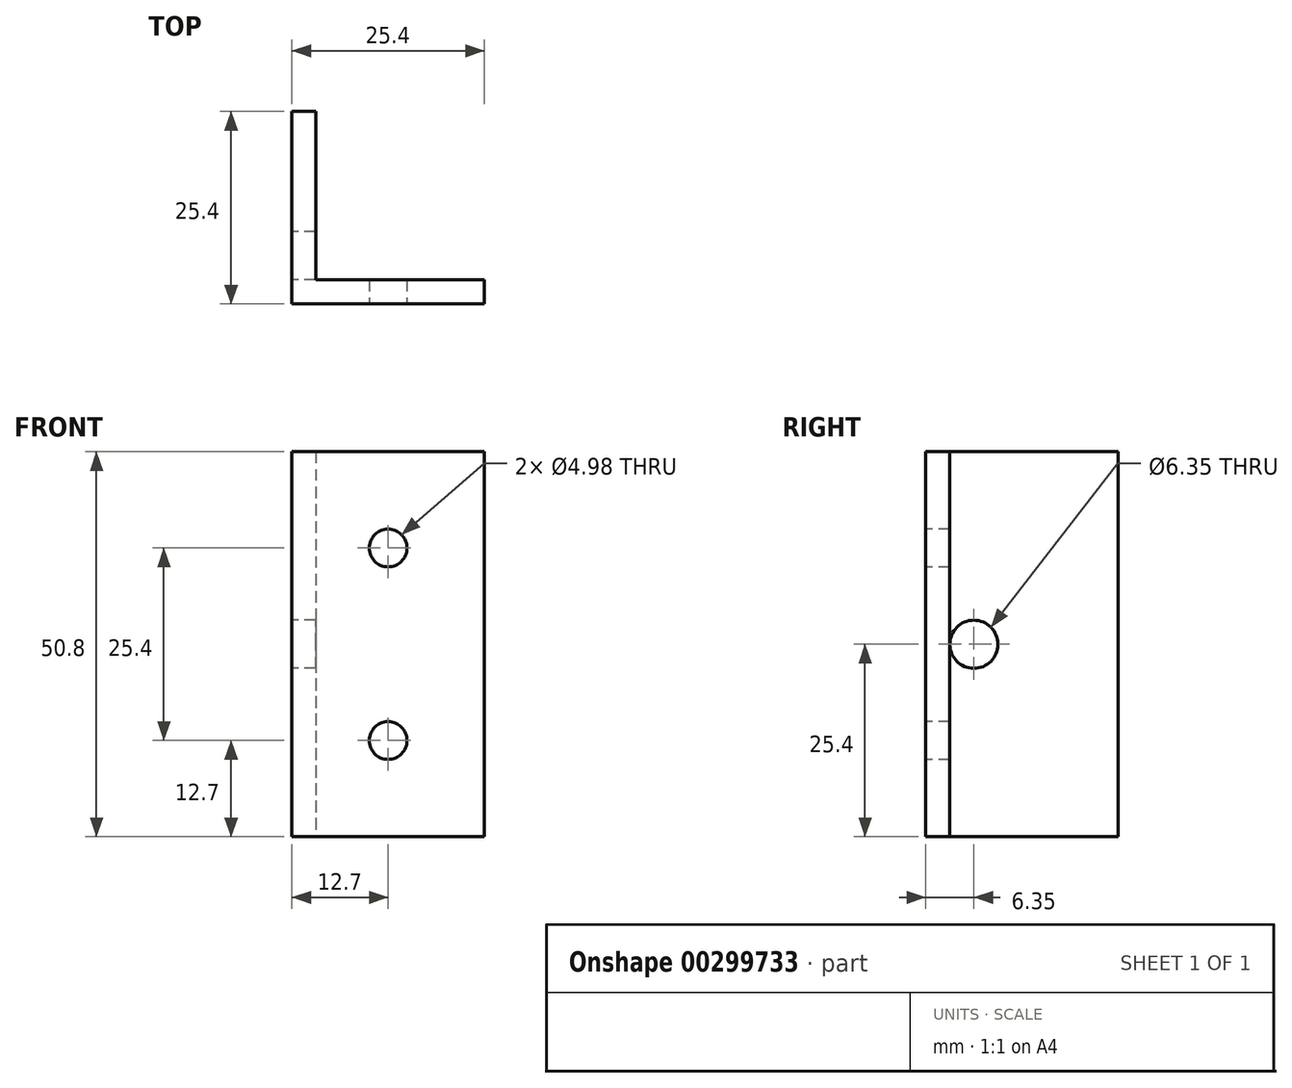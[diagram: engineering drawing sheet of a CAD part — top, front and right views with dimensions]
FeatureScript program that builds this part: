
annotation { "Feature Type Name" : "Feature", "Feature Type Description" : "" }
export const myFeature = defineFeature(function(context is Context, id is Id, definition is map)
    precondition{}
    {
        {
            var Q0;
            Q0=qCreatedBy(makeId("Top.planeOp"),FACE);
            var sketch = newSketch(context, id + "F0", { "sketchPlane" : qUnion([Q0])});
            skLineSegment(sketch, "E0", {"start": v(0, 25.4) * mm, "end": v(0, 0) * mm});
            skLineSegment(sketch, "E1", {"start": v(0, 0) * mm, "end": v(25.4, 0) * mm});
            skLineSegment(sketch, "E2", {"start": v(25.4, 0) * mm, "end": v(25.4, 3.18) * mm});
            skLineSegment(sketch, "E3", {"start": v(25.4, 3.18) * mm, "end": v(3.18, 3.17) * mm});
            skLineSegment(sketch, "E4", {"start": v(3.18, 3.17) * mm, "end": v(3.18, 25.4) * mm});
            skLineSegment(sketch, "E5", {"start": v(3.18, 25.4) * mm, "end": v(0, 25.4) * mm});
            skSolve(sketch);
        }
        {
            var Q0;
            Q0=makeQuery(id+"F0.imprint","IMPRINT",FACE,{"disambiguationData":[TD([[makeQuery(id+"F0.imprint","IMPRINT",EDGE,{"derivedFrom":sQuery(id+"F0.wireOp",EDGE,"E0")}),1.0]])]});
            extrude(context, id + "F1", {"entities" : qUnion([Q0]), "depth" : 50.8 * mm});
        }
        {
            var Q0;
            Q0=makeQuery(id+"F1.opExtrude","SWEPT_FACE",FACE,{"disambiguationData":[OSD([sQuery(id+"F0.wireOp",EDGE,"E1")])]});
            var sketch = newSketch(context, id + "F2", { "sketchPlane" : qUnion([Q0])});
            skCircle(sketch, "E6", {"center": v(12.7, 38.1) * mm, "radius": 2.49 * mm});
            skCircle(sketch, "E7", {"center": v(12.7, 12.7) * mm, "radius": 2.49 * mm});
            skSolve(sketch);
        }
        {
            var Q0;
            Q0 = qSketchRegion(id + "F2", true);
            extrude(context, id + "F3", {"entities" : qUnion([Q0]), "operationType" : NewBodyOperationType.REMOVE, "oppositeDirection" : true, "depth" : 25.4 * mm});
        }
        {
            var Q0;
            Q0=makeQuery(id+"F1.opExtrude","SWEPT_FACE",FACE,{"disambiguationData":[OSD([sQuery(id+"F0.wireOp",EDGE,"E0")])]});
            var sketch = newSketch(context, id + "F4", { "sketchPlane" : qUnion([Q0])});
            skCircle(sketch, "E8", {"center": v(-6.35, 25.4) * mm, "radius": 3.18 * mm});
            skSolve(sketch);
        }
        {
            var Q0;
            Q0=makeQuery(id+"F4.imprint","IMPRINT",FACE,{"disambiguationData":[TD([[makeQuery(id+"F4.imprint","IMPRINT",EDGE,{"derivedFrom":sQuery(id+"F4.wireOp",EDGE,"E8")}),1.0]])]});
            extrude(context, id + "F5", {"entities" : qUnion([Q0]), "operationType" : NewBodyOperationType.REMOVE, "oppositeDirection" : true, "depth" : 25.4 * mm});
        }
    });
